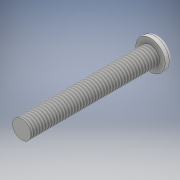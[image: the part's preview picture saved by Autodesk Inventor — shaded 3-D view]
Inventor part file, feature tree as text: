
AUTODESK INVENTOR PART (.ipt)
format: ipt  version: 2018 (Build 220112000, 112)  size: 143,360 bytes
history: native  units: mm
features: sketch x2, revolve x1, fillet x1, extrude x1, thread x1
ambient origin geometry x8: Origin, YZ Plane, XZ Plane, XY Plane, X Axis, Y Axis, Z Axis, Center Point
bodies: Solid1 (feature_tree)
feature tree (6):
  revolve  "Revolution1"  [1 undecoded]
  fillet  "Fillet1"  Radius=2.1mm
  extrude  "Extrusion1"  TaperAngle=90.0deg  [1 undecoded]
  thread  "Thread1"  [1 undecoded]
  sketch  "Sketch1"  dims[d0=2.5mm d1=35.0mm d2=2.1mm]
  sketch  "Sketch2"  dims[d3=4.0mm d4=90.0deg d5=1.0mm d6=0.75mm d7=0.75mm d8=2.7mm d9=2.7mm d10=40.0mm d12=360.0deg d14=1.0mm d15=0.0mm d16=10.0mm d17=0.0mm]
note: 3 required parameter values undecoded (feature->parameter linkage not recoverable at this tier; creation-order binding heuristic only, values carry confidence <= 0.55)